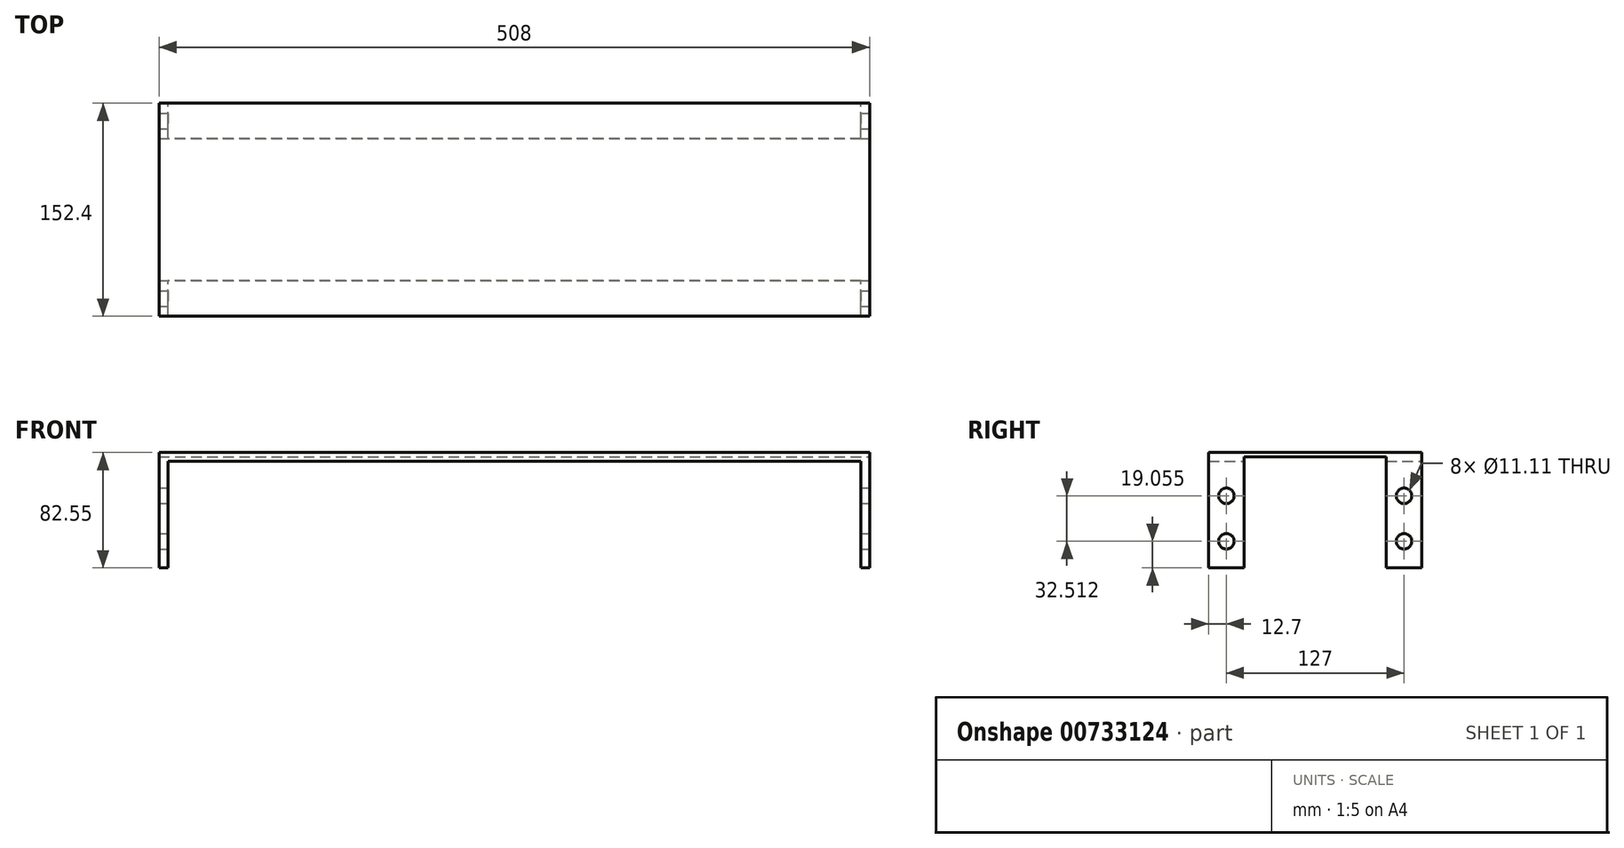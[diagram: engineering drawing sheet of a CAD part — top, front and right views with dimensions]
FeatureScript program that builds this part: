
annotation { "Feature Type Name" : "Feature", "Feature Type Description" : "" }
export const myFeature = defineFeature(function(context is Context, id is Id, definition is map)
    precondition{}
    {
        {
            var Q0;
            Q0=qCreatedBy(makeId("Front.planeOp"),FACE);
            var sketch = newSketch(context, id + "F0", { "sketchPlane" : qUnion([Q0])});
            skLineSegment(sketch, "E0.bottom", {"start": v(254, -3.17) * mm, "end": v(-254, -3.18) * mm});
            skLineSegment(sketch, "E0.top", {"start": v(254, 3.18) * mm, "end": v(-254, 3.18) * mm});
            skLineSegment(sketch, "E0.left", {"start": v(254, -3.17) * mm, "end": v(254, 3.18) * mm});
            skLineSegment(sketch, "E0.right", {"start": v(-254, -3.18) * mm, "end": v(-254, 3.17) * mm});
            skPoint(sketch, "E0.middle", {"position": v(0, 0) * mm});
            skSolve(sketch);
        }
        {
            var Q0;
            Q0 = qSketchRegion(id + "F0", true);
            extrude(context, id + "F1", {"entities" : qUnion([Q0]), "endBound" : BoundingType.SYMMETRIC, "depth" : 152.4 * mm, "offsetDistance" : 25.4 * mm});
        }
        {
            var Q0;
            Q0=qCreatedBy(makeId("Front.planeOp"),FACE);
            var sketch = newSketch(context, id + "F2", { "sketchPlane" : qUnion([Q0])});
            skLineSegment(sketch, "E1.bottom", {"start": v(-254, -3.18) * mm, "end": v(-247.65, -3.18) * mm});
            skLineSegment(sketch, "E1.top", {"start": v(-254, -79.38) * mm, "end": v(-247.65, -79.38) * mm});
            skLineSegment(sketch, "E1.left", {"start": v(-254, -3.18) * mm, "end": v(-254, -79.38) * mm});
            skLineSegment(sketch, "E1.right", {"start": v(-247.65, -3.18) * mm, "end": v(-247.65, -79.38) * mm});
            skLineSegment(sketch, "E2.bottom", {"start": v(254, -3.17) * mm, "end": v(247.65, -3.17) * mm});
            skLineSegment(sketch, "E2.top", {"start": v(254, -79.38) * mm, "end": v(247.65, -79.38) * mm});
            skLineSegment(sketch, "E2.left", {"start": v(254, -3.17) * mm, "end": v(254, -79.38) * mm});
            skLineSegment(sketch, "E2.right", {"start": v(247.65, -3.17) * mm, "end": v(247.65, -79.38) * mm});
            skSolve(sketch);
        }
        {
            var Q0;
            Q0 = qSketchRegion(id + "F2", true);
            extrude(context, id + "F3", {"entities" : qUnion([Q0]), "operationType" : NewBodyOperationType.ADD, "endBound" : BoundingType.SYMMETRIC, "depth" : 152.4 * mm, "offsetDistance" : 25.4 * mm});
        }
        {
            var Q0;
            Q0=qCreatedBy(makeId("Right.planeOp"),FACE);
            var sketch = newSketch(context, id + "F4", { "sketchPlane" : qUnion([Q0])});
            skLineSegment(sketch, "E3.bottom", {"start": v(-50.8, 0) * mm, "end": v(50.8, 0) * mm});
            skLineSegment(sketch, "E3.top", {"start": v(-50.8, -79.38) * mm, "end": v(50.8, -79.38) * mm});
            skLineSegment(sketch, "E3.left", {"start": v(-50.8, 0) * mm, "end": v(-50.8, -79.38) * mm});
            skLineSegment(sketch, "E3.right", {"start": v(50.8, 0) * mm, "end": v(50.8, -79.38) * mm});
            skSolve(sketch);
        }
        {
            var Q0;
            Q0 = qSketchRegion(id + "F4", true);
            extrude(context, id + "F5", {"entities" : qUnion([Q0]), "operationType" : NewBodyOperationType.REMOVE, "endBound" : BoundingType.THROUGH_ALL, "oppositeDirection" : true, "depth" : 25.4 * mm, "offsetDistance" : 25.4 * mm, "hasSecondDirection" : true, "secondDirectionBound" : SecondDirectionBoundingType.THROUGH_ALL, "secondDirectionOppositeDirection" : false, "secondDirectionDepth" : 25.4 * mm});
        }
        {
            var Q0;
            Q0=makeQuery(id+"F3.boolean.opBoolean","MERGE",FACE,{"derivedFrom":[makeQuery(id+"F1.opExtrude","SWEPT_FACE",FACE,{"disambiguationData":[OSD([sQuery(id+"F0.wireOp",EDGE,"E0.left")])]}),makeQuery(id+"F3.opExtrude","SWEPT_FACE",FACE,{"disambiguationData":[OSD([sQuery(id+"F2.wireOp",EDGE,"E2.left")])]})]});
            var sketch = newSketch(context, id + "F6", { "sketchPlane" : qUnion([Q0])});
            skLineSegment(sketch, "E4", {"start": v(-63.5, -79.38) * mm, "end": v(-63.5, -60.33) * mm, "construction": true});
            skLineSegment(sketch, "E5", {"start": v(-63.5, -60.33) * mm, "end": v(63.5, -60.33) * mm, "construction": true});
            skLineSegment(sketch, "E6", {"start": v(63.5, -60.33) * mm, "end": v(63.5, -79.38) * mm, "construction": true});
            skLineSegment(sketch, "E7", {"start": v(-63.5, -60.33) * mm, "end": v(-63.5, -27.81) * mm, "construction": true});
            skLineSegment(sketch, "E8", {"start": v(63.5, -60.33) * mm, "end": v(63.5, -27.81) * mm, "construction": true});
            skCircle(sketch, "E9", {"center": v(-63.5, -27.81) * mm, "radius": 5.56 * mm});
            skCircle(sketch, "E10", {"center": v(-63.5, -60.33) * mm, "radius": 5.56 * mm});
            skCircle(sketch, "E11", {"center": v(63.5, -27.81) * mm, "radius": 5.56 * mm});
            skCircle(sketch, "E12", {"center": v(63.5, -60.33) * mm, "radius": 5.56 * mm});
            skSolve(sketch);
        }
        {
            var Q0;
            Q0 = qSketchRegion(id + "F6", true);
            extrude(context, id + "F7", {"entities" : qUnion([Q0]), "operationType" : NewBodyOperationType.REMOVE, "endBound" : BoundingType.THROUGH_ALL, "oppositeDirection" : true, "depth" : 25.4 * mm, "offsetDistance" : 25.4 * mm});
        }
    });
